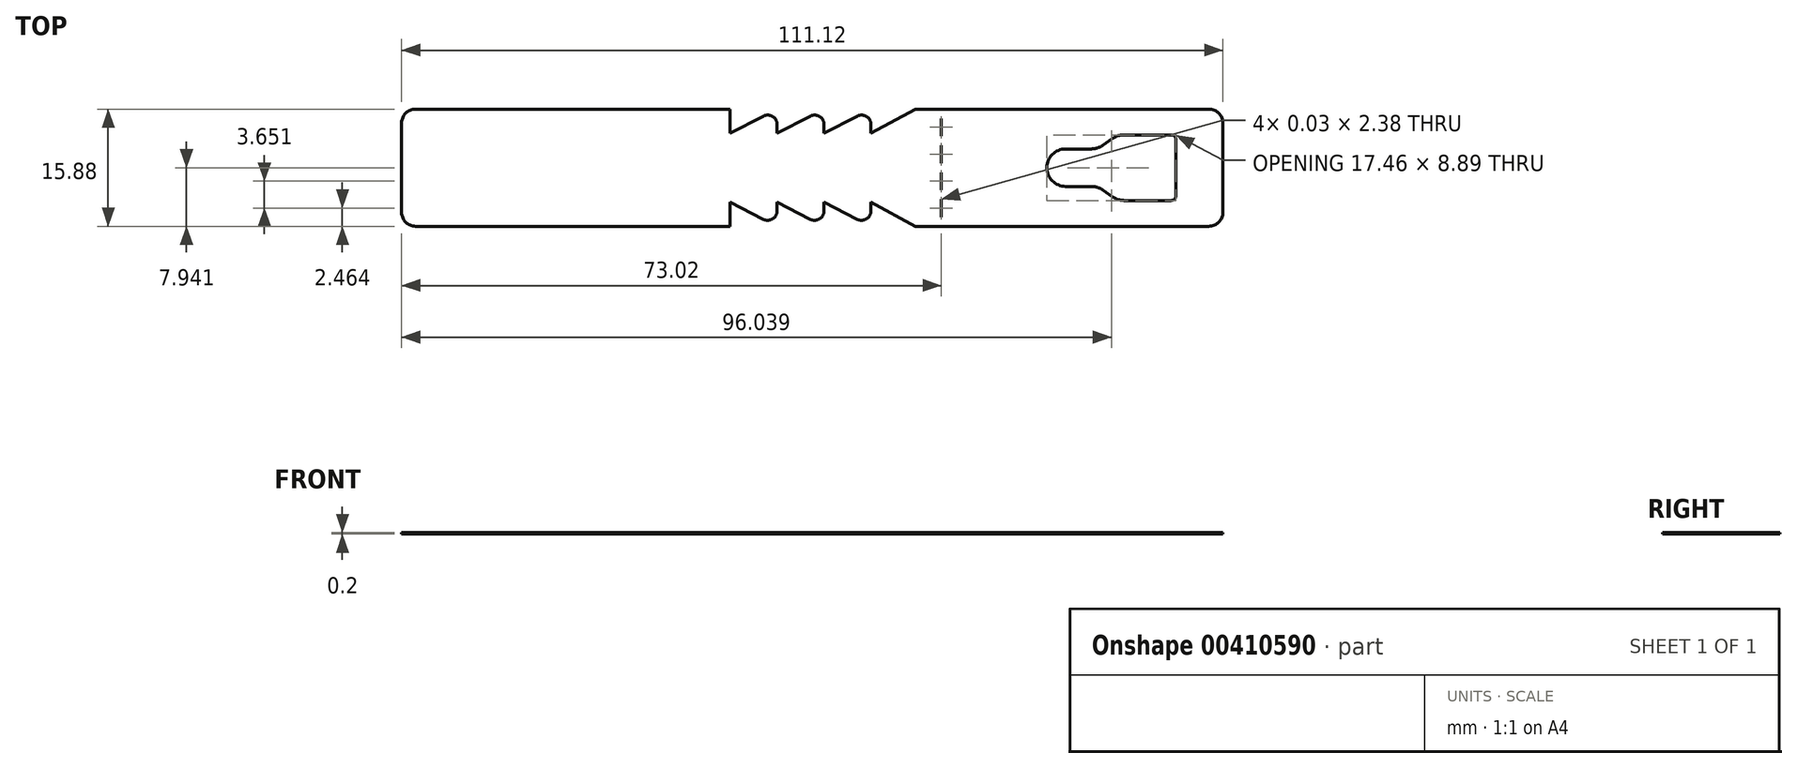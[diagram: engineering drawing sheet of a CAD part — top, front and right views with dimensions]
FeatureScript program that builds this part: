
annotation { "Feature Type Name" : "Feature", "Feature Type Description" : "" }
export const myFeature = defineFeature(function(context is Context, id is Id, definition is map)
    precondition{}
    {
        {
            var Q0;
            Q0=qCreatedBy(makeId("Top.planeOp"),FACE);
            var sketch = newSketch(context, id + "F0", { "sketchPlane" : qUnion([Q0])});
            skLineSegment(sketch, "E0.bottom", {"start": v(-85.9, 78.85) * mm, "end": v(-50.98, 78.85) * mm});
            skLineSegment(sketch, "E0.top", {"start": v(-85.9, 62.97) * mm, "end": v(-50.98, 62.97) * mm});
            skLineSegment(sketch, "E0.left", {"start": v(-87.81, 76.94) * mm, "end": v(-87.81, 64.88) * mm});
            skLineSegment(sketch, "E0.right", {"start": v(23.31, 76.94) * mm, "end": v(23.31, 64.88) * mm});
            skPoint(sketch, "E1", {"position": v(2.04, 70.91) * mm});
            skPoint(sketch, "E2", {"position": v(16.96, 70.91) * mm});
            skLineSegment(sketch, "E3", {"start": v(16.96, 74.72) * mm, "end": v(16.96, 67.1) * mm});
            skLineSegment(sketch, "E4", {"start": v(16.33, 66.47) * mm, "end": v(9.94, 66.47) * mm});
            skLineSegment(sketch, "E5", {"start": v(2.04, 68.37) * mm, "end": v(2.04, 73.45) * mm, "construction": true});
            skLineSegment(sketch, "E6", {"start": v(2.04, 73.45) * mm, "end": v(5.51, 73.45) * mm});
            skLineSegment(sketch, "E7", {"start": v(7.06, 73.94) * mm, "end": v(8.39, 74.87) * mm});
            skLineSegment(sketch, "E8", {"start": v(8.39, 66.96) * mm, "end": v(7.06, 67.88) * mm});
            skLineSegment(sketch, "E9", {"start": v(5.51, 68.37) * mm, "end": v(2.04, 68.37) * mm});
            skLineSegment(sketch, "E10", {"start": v(16.33, 75.36) * mm, "end": v(9.94, 75.36) * mm});
            skArc(sketch, "E11", {"start": v(2.04, 73.45) * mm, "mid": v(-0.5, 70.91) * mm, "end": v(2.04, 68.37) * mm});
            skPoint(sketch, "E12.visualSharp", {"position": v(16.96, 75.36) * mm});
            skArc(sketch, "E12.filletArc", {"start": v(16.96, 74.72) * mm, "mid": v(16.77, 75.17) * mm, "end": v(16.33, 75.36) * mm});
            skPoint(sketch, "E13.visualSharp", {"position": v(16.96, 66.47) * mm});
            skArc(sketch, "E13.filletArc", {"start": v(16.33, 66.47) * mm, "mid": v(16.77, 66.65) * mm, "end": v(16.96, 67.1) * mm});
            skPoint(sketch, "E14", {"position": v(-0.5, 70.91) * mm});
            skPoint(sketch, "E15.visualSharp", {"position": v(9.09, 75.36) * mm});
            skArc(sketch, "E15.filletArc", {"start": v(9.94, 75.36) * mm, "mid": v(9.13, 75.23) * mm, "end": v(8.39, 74.87) * mm});
            skPoint(sketch, "E16.visualSharp", {"position": v(6.37, 73.45) * mm});
            skArc(sketch, "E16.filletArc", {"start": v(5.51, 73.45) * mm, "mid": v(6.33, 73.58) * mm, "end": v(7.06, 73.94) * mm});
            skPoint(sketch, "E17.visualSharp", {"position": v(6.37, 68.37) * mm});
            skArc(sketch, "E17.filletArc", {"start": v(7.06, 67.88) * mm, "mid": v(6.33, 68.25) * mm, "end": v(5.51, 68.37) * mm});
            skPoint(sketch, "E18.visualSharp", {"position": v(9.09, 66.47) * mm});
            skArc(sketch, "E18.filletArc", {"start": v(8.39, 66.96) * mm, "mid": v(9.13, 66.6) * mm, "end": v(9.94, 66.47) * mm});
            skLineSegment(sketch, "E19", {"start": v(-37.01, 75.58) * mm, "end": v(-32.52, 77.9) * mm});
            skLineSegment(sketch, "E20", {"start": v(-37.01, 66.24) * mm, "end": v(-32.52, 63.93) * mm});
            skLineSegment(sketch, "E21", {"start": v(-37.01, 66.24) * mm, "end": v(-37.01, 65.05) * mm});
            skLineSegment(sketch, "E22", {"start": v(-37.01, 75.58) * mm, "end": v(-37.01, 76.77) * mm});
            skLineSegment(sketch, "E23.trimOffspring", {"start": v(-18.28, 62.97) * mm, "end": v(21.4, 62.97) * mm});
            skLineSegment(sketch, "E24", {"start": v(-38.87, 63.93) * mm, "end": v(-43.36, 66.24) * mm});
            skLineSegment(sketch, "E25", {"start": v(-43.36, 66.24) * mm, "end": v(-43.36, 65.05) * mm});
            skLineSegment(sketch, "E26", {"start": v(-38.87, 77.9) * mm, "end": v(-43.36, 75.58) * mm});
            skLineSegment(sketch, "E27", {"start": v(-43.36, 75.58) * mm, "end": v(-43.36, 76.77) * mm});
            skLineSegment(sketch, "E28", {"start": v(-45.22, 77.9) * mm, "end": v(-49.71, 75.58) * mm, "construction": true});
            skLineSegment(sketch, "E29", {"start": v(-49.71, 75.58) * mm, "end": v(-49.71, 77.58) * mm, "construction": true});
            skLineSegment(sketch, "E30", {"start": v(-45.22, 63.93) * mm, "end": v(-49.71, 66.24) * mm, "construction": true});
            skLineSegment(sketch, "E31", {"start": v(-49.71, 66.24) * mm, "end": v(-49.71, 64.24) * mm, "construction": true});
            skPoint(sketch, "E32.visualSharp", {"position": v(-87.81, 78.85) * mm});
            skArc(sketch, "E32.filletArc", {"start": v(-85.9, 78.85) * mm, "mid": v(-87.26, 78.3) * mm, "end": v(-87.81, 76.94) * mm});
            skPoint(sketch, "E33.visualSharp", {"position": v(-87.81, 62.97) * mm});
            skArc(sketch, "E33.filletArc", {"start": v(-87.81, 64.88) * mm, "mid": v(-87.26, 63.53) * mm, "end": v(-85.9, 62.97) * mm});
            skPoint(sketch, "E34.visualSharp", {"position": v(23.31, 62.97) * mm});
            skArc(sketch, "E34.filletArc", {"start": v(21.4, 62.97) * mm, "mid": v(22.75, 63.53) * mm, "end": v(23.31, 64.88) * mm});
            skPoint(sketch, "E35.visualSharp", {"position": v(23.31, 78.3) * mm});
            skArc(sketch, "E35.filletArc", {"start": v(23.31, 76.94) * mm, "mid": v(22.75, 78.3) * mm, "end": v(21.4, 78.85) * mm});
            skLineSegment(sketch, "E36", {"start": v(-14.79, 78.85) * mm, "end": v(-14.79, 62.97) * mm, "construction": true});
            skLineSegment(sketch, "E37", {"start": v(-30.66, 65.05) * mm, "end": v(-30.66, 66.24) * mm});
            skLineSegment(sketch, "E38", {"start": v(-30.66, 66.24) * mm, "end": v(-26.17, 63.93) * mm});
            skLineSegment(sketch, "E39", {"start": v(-30.66, 76.77) * mm, "end": v(-30.66, 75.58) * mm});
            skLineSegment(sketch, "E40", {"start": v(-30.66, 75.58) * mm, "end": v(-26.17, 77.9) * mm});
            skLineSegment(sketch, "E41", {"start": v(-24.31, 76.77) * mm, "end": v(-24.31, 75.58) * mm});
            skLineSegment(sketch, "E42", {"start": v(-24.31, 75.58) * mm, "end": v(-18.28, 78.85) * mm});
            skLineSegment(sketch, "E43", {"start": v(-24.31, 65.05) * mm, "end": v(-24.31, 66.24) * mm});
            skLineSegment(sketch, "E44", {"start": v(-24.31, 66.24) * mm, "end": v(-18.28, 62.97) * mm});
            skLineSegment(sketch, "E45.trimOffspring", {"start": v(-18.28, 78.85) * mm, "end": v(21.4, 78.85) * mm});
            skPoint(sketch, "E46.visualSharp", {"position": v(-49.71, 78.85) * mm});
            skArc(sketch, "E46.filletArc", {"start": v(-49.71, 77.58) * mm, "mid": v(-50.09, 78.48) * mm, "end": v(-50.98, 78.85) * mm, "construction": true});
            skPoint(sketch, "E47.visualSharp", {"position": v(-43.36, 78.85) * mm});
            skArc(sketch, "E47.filletArc", {"start": v(-43.36, 76.77) * mm, "mid": v(-43.97, 77.85) * mm, "end": v(-45.22, 77.9) * mm, "construction": true});
            skPoint(sketch, "E48.visualSharp", {"position": v(-37.01, 78.85) * mm});
            skArc(sketch, "E48.filletArc", {"start": v(-37.01, 76.77) * mm, "mid": v(-37.62, 77.85) * mm, "end": v(-38.87, 77.9) * mm});
            skPoint(sketch, "E49.visualSharp", {"position": v(-30.66, 78.85) * mm});
            skArc(sketch, "E49.filletArc", {"start": v(-30.66, 76.77) * mm, "mid": v(-31.27, 77.85) * mm, "end": v(-32.52, 77.9) * mm});
            skPoint(sketch, "E50.visualSharp", {"position": v(-24.31, 78.85) * mm});
            skArc(sketch, "E50.filletArc", {"start": v(-24.31, 76.77) * mm, "mid": v(-24.92, 77.85) * mm, "end": v(-26.17, 77.9) * mm});
            skPoint(sketch, "E51.visualSharp", {"position": v(-24.31, 62.97) * mm});
            skArc(sketch, "E51.filletArc", {"start": v(-26.17, 63.93) * mm, "mid": v(-24.92, 63.97) * mm, "end": v(-24.31, 65.05) * mm});
            skPoint(sketch, "E52.visualSharp", {"position": v(-30.66, 62.97) * mm});
            skArc(sketch, "E52.filletArc", {"start": v(-32.52, 63.93) * mm, "mid": v(-31.27, 63.97) * mm, "end": v(-30.66, 65.05) * mm});
            skPoint(sketch, "E53.visualSharp", {"position": v(-37.01, 62.97) * mm});
            skArc(sketch, "E53.filletArc", {"start": v(-38.87, 63.93) * mm, "mid": v(-37.62, 63.97) * mm, "end": v(-37.01, 65.05) * mm});
            skPoint(sketch, "E54.visualSharp", {"position": v(-43.36, 62.97) * mm});
            skArc(sketch, "E54.filletArc", {"start": v(-45.22, 63.93) * mm, "mid": v(-43.97, 63.97) * mm, "end": v(-43.36, 65.05) * mm, "construction": true});
            skPoint(sketch, "E55.visualSharp", {"position": v(-49.71, 62.97) * mm});
            skArc(sketch, "E55.filletArc", {"start": v(-50.98, 62.97) * mm, "mid": v(-50.09, 63.35) * mm, "end": v(-49.71, 64.24) * mm, "construction": true});
            skLineSegment(sketch, "E56", {"start": v(-50.98, 78.85) * mm, "end": v(-43.36, 78.85) * mm});
            skLineSegment(sketch, "E57", {"start": v(-43.36, 76.77) * mm, "end": v(-43.36, 78.85) * mm});
            skLineSegment(sketch, "E58", {"start": v(-43.36, 65.05) * mm, "end": v(-43.36, 62.97) * mm});
            skLineSegment(sketch, "E59", {"start": v(-50.98, 62.97) * mm, "end": v(-43.36, 62.97) * mm});
            skLineSegment(sketch, "E60", {"start": v(23.31, 70.91) * mm, "end": v(-87.81, 70.91) * mm, "construction": true});
            skPoint(sketch, "E60.endSnap0", {"position": v(-87.81, 70.91) * mm});
            skLineSegment(sketch, "E61", {"start": v(-24.31, 75.58) * mm, "end": v(-49.71, 75.58) * mm, "construction": true});
            skLineSegment(sketch, "E62", {"start": v(-49.71, 66.24) * mm, "end": v(-24.31, 66.24) * mm, "construction": true});
            skLineSegment(sketch, "E63", {"start": v(-49.71, 66.24) * mm, "end": v(-49.71, 75.58) * mm, "construction": true});
            skPoint(sketch, "E64", {"position": v(-49.71, 70.91) * mm});
            skLineSegment(sketch, "E65", {"start": v(-25.58, 65.05) * mm, "end": v(-25.58, 76.77) * mm, "construction": true});
            skLineSegment(sketch, "E66", {"start": v(-38.28, 76.77) * mm, "end": v(-38.28, 65.05) * mm, "construction": true});
            skLineSegment(sketch, "E67", {"start": v(-44.63, 65.05) * mm, "end": v(-44.63, 76.77) * mm, "construction": true});
            skPoint(sketch, "E68", {"position": v(-25.58, 70.91) * mm});
            skPoint(sketch, "E69", {"position": v(-31.93, 70.91) * mm});
            skPoint(sketch, "E70", {"position": v(-38.28, 70.91) * mm});
            skPoint(sketch, "E71", {"position": v(-44.63, 70.91) * mm});
            skLineSegment(sketch, "E72", {"start": v(-31.93, 65.05) * mm, "end": v(-31.93, 76.77) * mm, "construction": true});
            skSolve(sketch);
        }
        {
            var Q0;
            Q0 = qSketchRegion(id + "F0", true);
            extrude(context, id + "F1", {"entities" : qUnion([Q0]), "offsetDistance" : 25.4 * mm, "depth" : 0.2 * mm});
        }
        {
            var Q0;
            Q0=makeQuery(id+"F1.opExtrude","CAP_FACE",FACE,{"disambiguationData":[OSD([sQuery(id+"F0.wireOp",EDGE,"E0.bottom"),sQuery(id+"F0.wireOp",EDGE,"E0.top"),sQuery(id+"F0.wireOp",EDGE,"E0.left"),sQuery(id+"F0.wireOp",EDGE,"E0.right"),sQuery(id+"F0.wireOp",EDGE,"E3"),sQuery(id+"F0.wireOp",EDGE,"E4"),sQuery(id+"F0.wireOp",EDGE,"E6"),sQuery(id+"F0.wireOp",EDGE,"E7"),sQuery(id+"F0.wireOp",EDGE,"E8"),sQuery(id+"F0.wireOp",EDGE,"E9"),sQuery(id+"F0.wireOp",EDGE,"E10"),sQuery(id+"F0.wireOp",EDGE,"E11"),sQuery(id+"F0.wireOp",EDGE,"E12.filletArc"),sQuery(id+"F0.wireOp",EDGE,"E13.filletArc"),sQuery(id+"F0.wireOp",EDGE,"E15.filletArc"),sQuery(id+"F0.wireOp",EDGE,"E16.filletArc"),sQuery(id+"F0.wireOp",EDGE,"E17.filletArc"),sQuery(id+"F0.wireOp",EDGE,"E18.filletArc"),sQuery(id+"F0.wireOp",EDGE,"E19"),sQuery(id+"F0.wireOp",EDGE,"E20"),sQuery(id+"F0.wireOp",EDGE,"E21"),sQuery(id+"F0.wireOp",EDGE,"E22"),sQuery(id+"F0.wireOp",EDGE,"E23.trimOffspring"),sQuery(id+"F0.wireOp",EDGE,"E24"),sQuery(id+"F0.wireOp",EDGE,"E25"),sQuery(id+"F0.wireOp",EDGE,"E26"),sQuery(id+"F0.wireOp",EDGE,"E27"),sQuery(id+"F0.wireOp",EDGE,"E28"),sQuery(id+"F0.wireOp",EDGE,"E29"),sQuery(id+"F0.wireOp",EDGE,"E30"),sQuery(id+"F0.wireOp",EDGE,"E31"),sQuery(id+"F0.wireOp",EDGE,"E32.filletArc"),sQuery(id+"F0.wireOp",EDGE,"E33.filletArc"),sQuery(id+"F0.wireOp",EDGE,"E34.filletArc"),sQuery(id+"F0.wireOp",EDGE,"E35.filletArc"),sQuery(id+"F0.wireOp",EDGE,"E37"),sQuery(id+"F0.wireOp",EDGE,"E38"),sQuery(id+"F0.wireOp",EDGE,"E39"),sQuery(id+"F0.wireOp",EDGE,"E40"),sQuery(id+"F0.wireOp",EDGE,"E41"),sQuery(id+"F0.wireOp",EDGE,"E42"),sQuery(id+"F0.wireOp",EDGE,"E43"),sQuery(id+"F0.wireOp",EDGE,"E44"),sQuery(id+"F0.wireOp",EDGE,"E45.trimOffspring")])],"isStart":false});
            var sketch = newSketch(context, id + "F2", { "sketchPlane" : qUnion([Q0])});
            skLineSegment(sketch, "E73.bottom", {"start": v(-14.8, 77.58) * mm, "end": v(-14.78, 77.58) * mm});
            skLineSegment(sketch, "E73.top", {"start": v(-14.8, 75.2) * mm, "end": v(-14.78, 75.2) * mm});
            skLineSegment(sketch, "E73.left", {"start": v(-14.8, 77.58) * mm, "end": v(-14.8, 75.2) * mm});
            skLineSegment(sketch, "E73.right", {"start": v(-14.78, 77.58) * mm, "end": v(-14.78, 75.2) * mm});
            skLineSegment(sketch, "E74", {"start": v(-14.79, 75.2) * mm, "end": v(-14.79, 73.93) * mm, "construction": true});
            skLineSegment(sketch, "E75", {"start": v(-14.79, 77.58) * mm, "end": v(-14.79, 78.85) * mm, "construction": true});
            skLineSegment(sketch, "E76.bottom", {"start": v(-14.8, 73.93) * mm, "end": v(-14.78, 73.93) * mm});
            skLineSegment(sketch, "E76.top", {"start": v(-14.8, 71.55) * mm, "end": v(-14.78, 71.55) * mm});
            skLineSegment(sketch, "E76.left", {"start": v(-14.8, 73.93) * mm, "end": v(-14.8, 71.55) * mm});
            skLineSegment(sketch, "E76.right", {"start": v(-14.78, 73.93) * mm, "end": v(-14.78, 71.55) * mm});
            skLineSegment(sketch, "E77", {"start": v(-14.79, 71.55) * mm, "end": v(-14.79, 70.28) * mm, "construction": true});
            skLineSegment(sketch, "E78.bottom", {"start": v(-14.8, 70.28) * mm, "end": v(-14.78, 70.28) * mm});
            skLineSegment(sketch, "E78.top", {"start": v(-14.8, 67.9) * mm, "end": v(-14.78, 67.9) * mm});
            skLineSegment(sketch, "E78.left", {"start": v(-14.8, 70.28) * mm, "end": v(-14.8, 67.9) * mm});
            skLineSegment(sketch, "E78.right", {"start": v(-14.78, 70.28) * mm, "end": v(-14.78, 67.9) * mm});
            skLineSegment(sketch, "E79", {"start": v(-14.79, 67.9) * mm, "end": v(-14.79, 66.62) * mm, "construction": true});
            skLineSegment(sketch, "E80.bottom", {"start": v(-14.8, 66.62) * mm, "end": v(-14.78, 66.62) * mm});
            skLineSegment(sketch, "E80.top", {"start": v(-14.8, 64.24) * mm, "end": v(-14.78, 64.24) * mm});
            skLineSegment(sketch, "E80.left", {"start": v(-14.8, 66.62) * mm, "end": v(-14.8, 64.24) * mm});
            skLineSegment(sketch, "E80.right", {"start": v(-14.78, 66.62) * mm, "end": v(-14.78, 64.24) * mm});
            skLineSegment(sketch, "E81", {"start": v(-14.79, 64.24) * mm, "end": v(-14.79, 62.97) * mm, "construction": true});
            skSolve(sketch);
        }
        {
            var Q0;
            Q0 = qSketchRegion(id + "F2", true);
            extrude(context, id + "F3", {"entities" : qUnion([Q0]), "operationType" : NewBodyOperationType.REMOVE, "oppositeDirection" : true, "depth" : 25.4 * mm});
        }
    });
